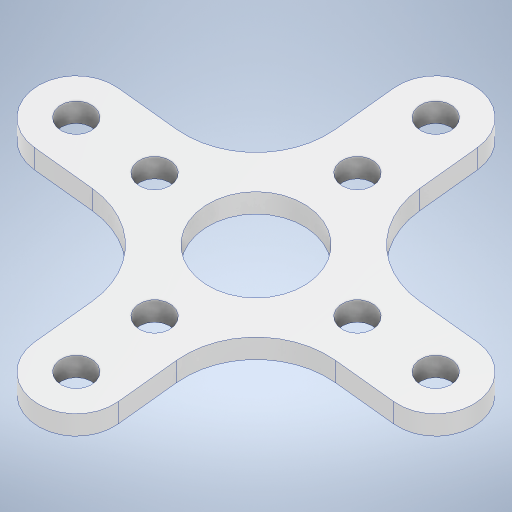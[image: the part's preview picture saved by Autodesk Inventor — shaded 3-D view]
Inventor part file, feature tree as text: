
AUTODESK INVENTOR PART (.ipt)
format: ipt  version: 2024 (Build 280153000, 153)  size: 301,056 bytes
history: native  units: in
note: dims shown in document units (in); Inventor stores cm internally (conversion verified against a paired STEP export)
features: extrude x3, sketch x3, projected_geometry x1
ambient origin geometry x8: Origin, YZ Plane, XZ Plane, XY Plane, X Axis, Y Axis, Z Axis, Center Point
bodies: Solid1 (feature_tree)
feature tree (7):
  extrude  "Extrusion1"  Depth=1.2087in
  extrude  "Extrusion2"  Depth=0.3in
  extrude  "Extrusion3"  TaperAngle=0.0deg  [1 undecoded]
  sketch  "Sketch1"  dims[d0=1.2087in d1=1.2087in]
  sketch  "Sketch2"  dims[d2=0.08in d3=0.0in d4=0.3in]
  sketch  "Sketch3"  dims[d5=0.66in d6=0.0in d7=0.0in d8=0.12in d9=0.12in d10=0.4in d11=0.38in d12=1.5748in d14=360.0deg d16=1.0in d17=0.0in]
  projected_geometry  "Projected Loop1"
note: 1 required parameter value undecoded (feature->parameter linkage not recoverable at this tier; creation-order binding heuristic only, values carry confidence <= 0.55)
